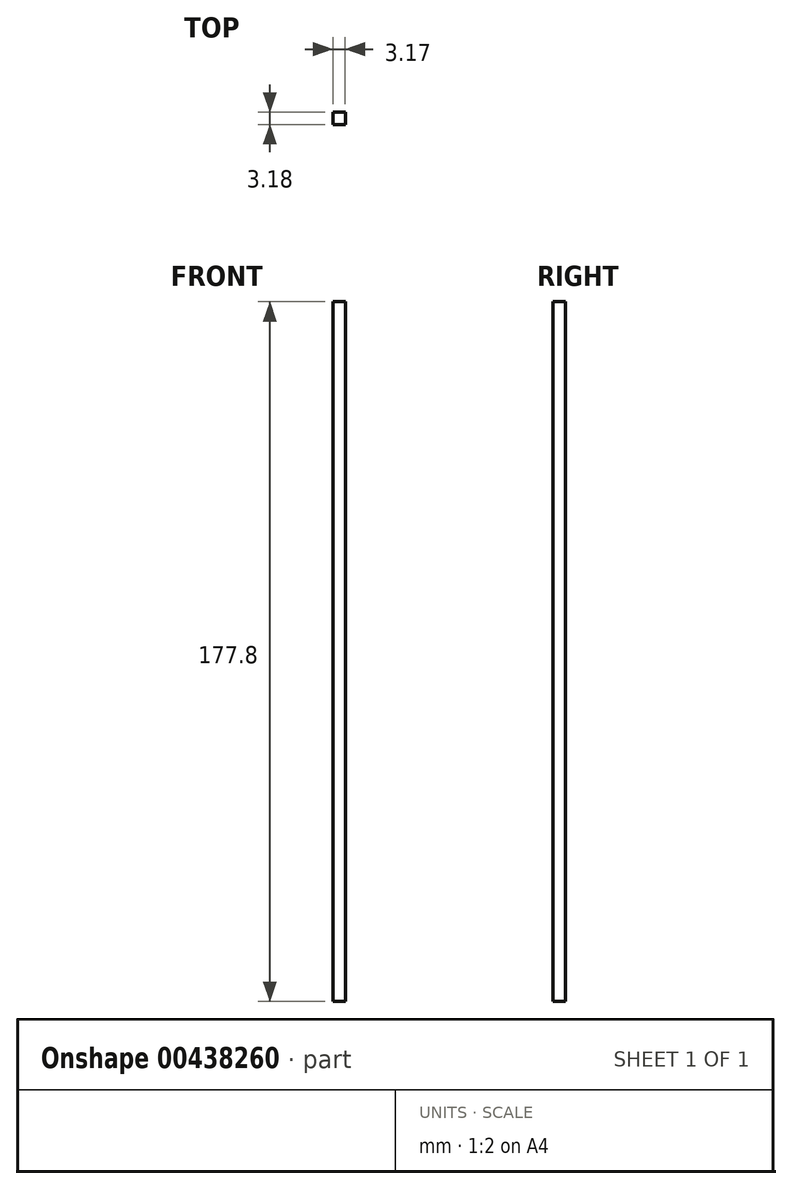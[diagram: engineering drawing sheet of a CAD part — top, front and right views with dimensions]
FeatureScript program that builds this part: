
annotation { "Feature Type Name" : "Feature", "Feature Type Description" : "" }
export const myFeature = defineFeature(function(context is Context, id is Id, definition is map)
    precondition{}
    {
        {
            var Q0;
            Q0=qCreatedBy(makeId("Right.planeOp"),FACE);
            var sketch = newSketch(context, id + "F0", { "sketchPlane" : qUnion([Q0])});
            skLineSegment(sketch, "E0.bottom", {"start": v(-30.63, 147.33) * mm, "end": v(-33.8, 147.33) * mm});
            skLineSegment(sketch, "E0.top", {"start": v(-30.63, -30.47) * mm, "end": v(-33.8, -30.47) * mm});
            skLineSegment(sketch, "E0.left", {"start": v(-30.63, 147.33) * mm, "end": v(-30.63, -30.47) * mm});
            skLineSegment(sketch, "E0.right", {"start": v(-33.8, 147.33) * mm, "end": v(-33.8, -30.47) * mm});
            skSolve(sketch);
        }
        {
            var Q0;
            Q0 = qSketchRegion(id + "F0", true);
            extrude(context, id + "F1", {"entities" : qUnion([Q0]), "depth" : 3.17 * mm});
        }
    });
